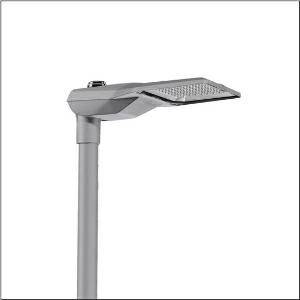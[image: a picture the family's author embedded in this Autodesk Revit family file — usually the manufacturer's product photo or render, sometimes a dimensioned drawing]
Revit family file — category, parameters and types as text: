
# Revit family: streetlight_sl_21_midi___st1_0a_5xe7d67n08nb_5be6
name_source: partatom
category: Lighting Fixtures
units: mm (PartAtom-declared; Revit-internal decimal feet)

## family parameters
Cut with Voids When Loaded = No
Host = Face
Light Source = No
Part Type = Normal
Room Calculation Point = No
Round Connector Dimension = Use Diameter
Shared = No

## types (1)
- --- (1 x LED, 20350 lm, 151.2 W, 2700K)
    Apparent Load = 151 VA
    CIE Flux Codes = 40 73 97 100 100
    Color Rendering = 70
    Color Temperature = 2700K
    Default Elevation = 1800 mm
    Description = Streetlight SL 21 midi, mast luminaire, primary light control with lens, of PMMA, primary optical cover: cover, of toughened safety glass, transparent, light distribution: ST1.0a, light emission: direct distribution, primary light characteristic: asymmetric, installation type: side-entry, LED, 3G 2.5mm², High Power LED, rated luminous flux: 20.350lm, luminous efficacy: 135lm/W, light colour: 727, colour temperature: 2700K, control: overheat protection, pre-setting: linear dimming characteristic, constant luminous flux control, time-dependent luminous flux control, flexible luminous flux parameterisation, mains connection: 220..240V, AC, 50/60Hz, connection cable pre-assembled, cable length: 12,5m, wiring characteristics: H05VV-F, start of lifetime: 151W, end of service life: 157W, reduction: 70W, luminaire housing, of diecast aluminium (EN AC-44300), powder-coated, Siteco® metallic grey (DB 702S), corrosivity category C5 mid according to DIN EN ISO 12944, multi-level sealing system, sealing non-destructively replaceable, inclination adjustable: 0°, 5°, 10°, 15°, length: 644mm, width: 335mm, height: 110mm, spigot size: 42mm (side-entry), protection rating (complete): IP66, insulation class (complete): insulation class I (protective earthing), certification: CE, ENEC, ENEC+, VDE, impact resistance: IK09, permissible operating ambient temperature for outdoor applications: -40..+50°C, standard-compliant lighting for roads and squares, packaging unit: 1 piece

Light Distribution: ST1.0a
    Height = 111 mm
    Lamp = 1 x LED
    Lamp Light Flux = 20350 lm
    Lamp Power = 151.2 W
    Lamp count = 1
    Length = 644 mm
    Luminous efficacy = 135 lm/W
    Manufacturer = Siteco
    ModVariant = No
    Model = 5XE7D67N08NB
    Number of Poles = 1
    OnlyDefault = Yes
    Power Factor = 1
    Product Name = Streetlight SL 21 midi | ST1.0a
    Product group = mast luminaire | pylon top
    ProductGroupID = 6100
    Protection Class = Protection class I
    Protection Degree = IP 66
    RLX_Detail_Level = 1
    RLX_Emergency_Light_Flux = 0 lm
    RLX_Emergency_Type = 0
    RLX_Emergency_Type_DB = No
    RlxData = <blob elided: 90425 chars, md5=c605f575>
    Socket = socket
    Standby Power = 0 W
    System Light Flux = 20350 lm
    System Power = 151 W
    Type Comments = factory setting: luminous flux: 100 % | dim-lin: 254 | 802 mA
    Type Image = l_1294377.jpg
    URL = http://relux.com
    VarID = @adj_104855
    Voltage = 0 V
    Weight = 0.00 kg
    Width = 336 mm

## geometry (parser evidence)
native form markers: Blend x4, Sweep x12
no freeform markers — native parametric forms only
